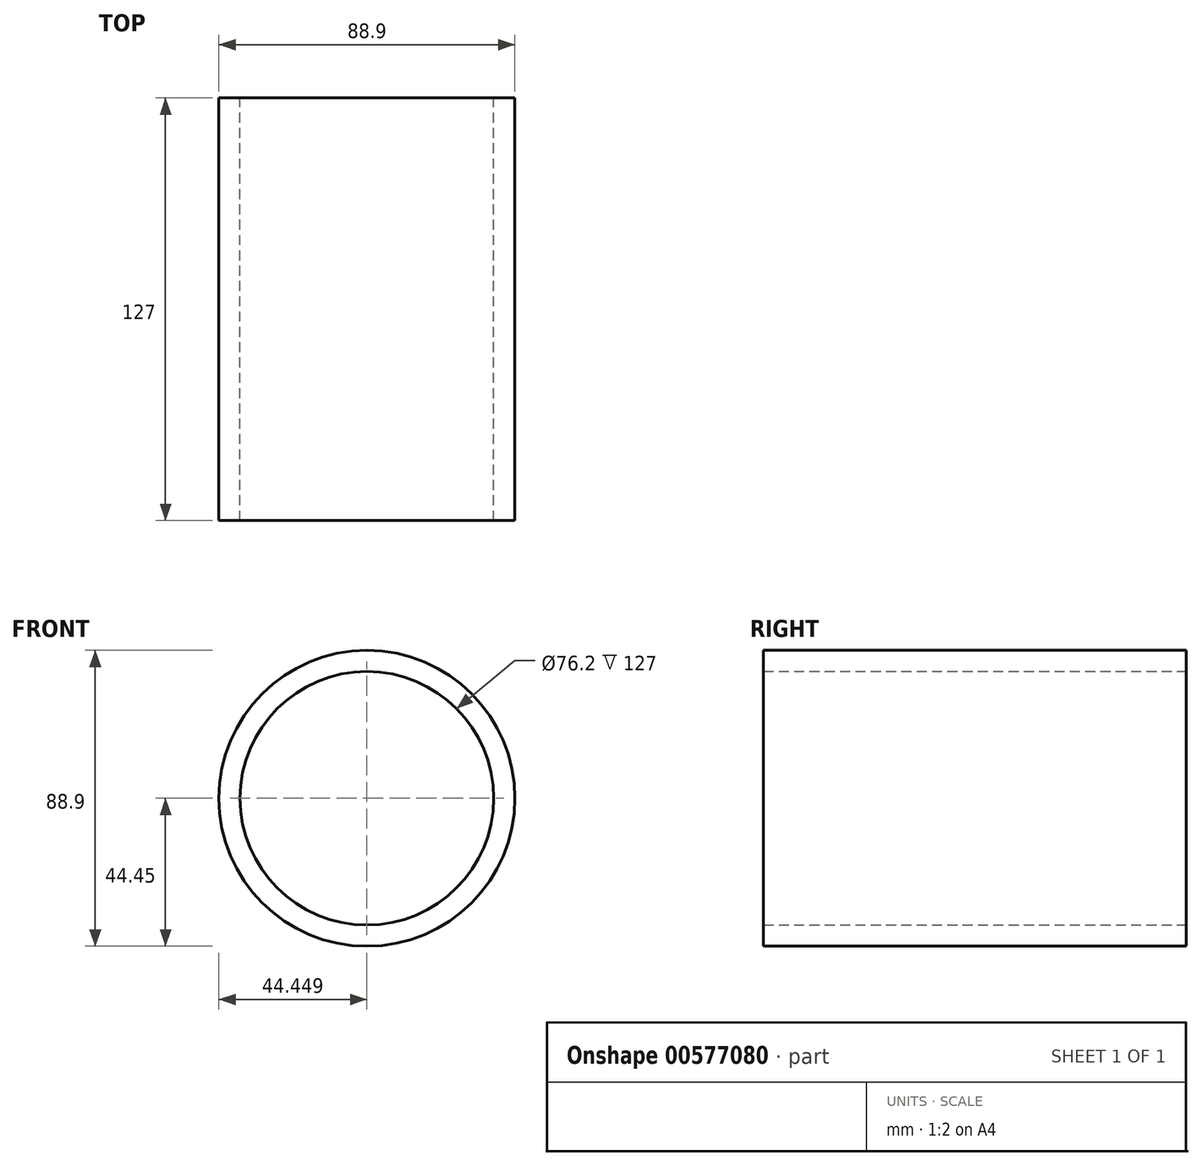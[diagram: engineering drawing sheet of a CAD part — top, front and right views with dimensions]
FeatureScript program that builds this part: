
annotation { "Feature Type Name" : "Feature", "Feature Type Description" : "" }
export const myFeature = defineFeature(function(context is Context, id is Id, definition is map)
    precondition{}
    {
        {
            var Q0;
            Q0=qCreatedBy(makeId("Front.planeOp"),FACE);
            var sketch = newSketch(context, id + "F0", { "sketchPlane" : qUnion([Q0])});
            skCircle(sketch, "E0", {"center": v(-8.12, 0) * mm, "radius": 44.45 * mm});
            skCircle(sketch, "E1", {"center": v(-8.12, 0) * mm, "radius": 38.1 * mm});
            skCircle(sketch, "E2", {"center": v(-8.12, 0) * mm, "radius": 31.75 * mm});
            skCircle(sketch, "E3", {"center": v(-8.12, 0) * mm, "radius": 25.4 * mm});
            skSolve(sketch);
        }
        {
            var Q0;
            Q0 = qSketchRegion(id + "F0", true);
            extrude(context, id + "F1", {"entities" : qUnion([Q0]), "endBound" : BoundingType.SYMMETRIC, "depth" : 127 * mm, "offsetDistance" : 25.4 * mm});
        }
    });
